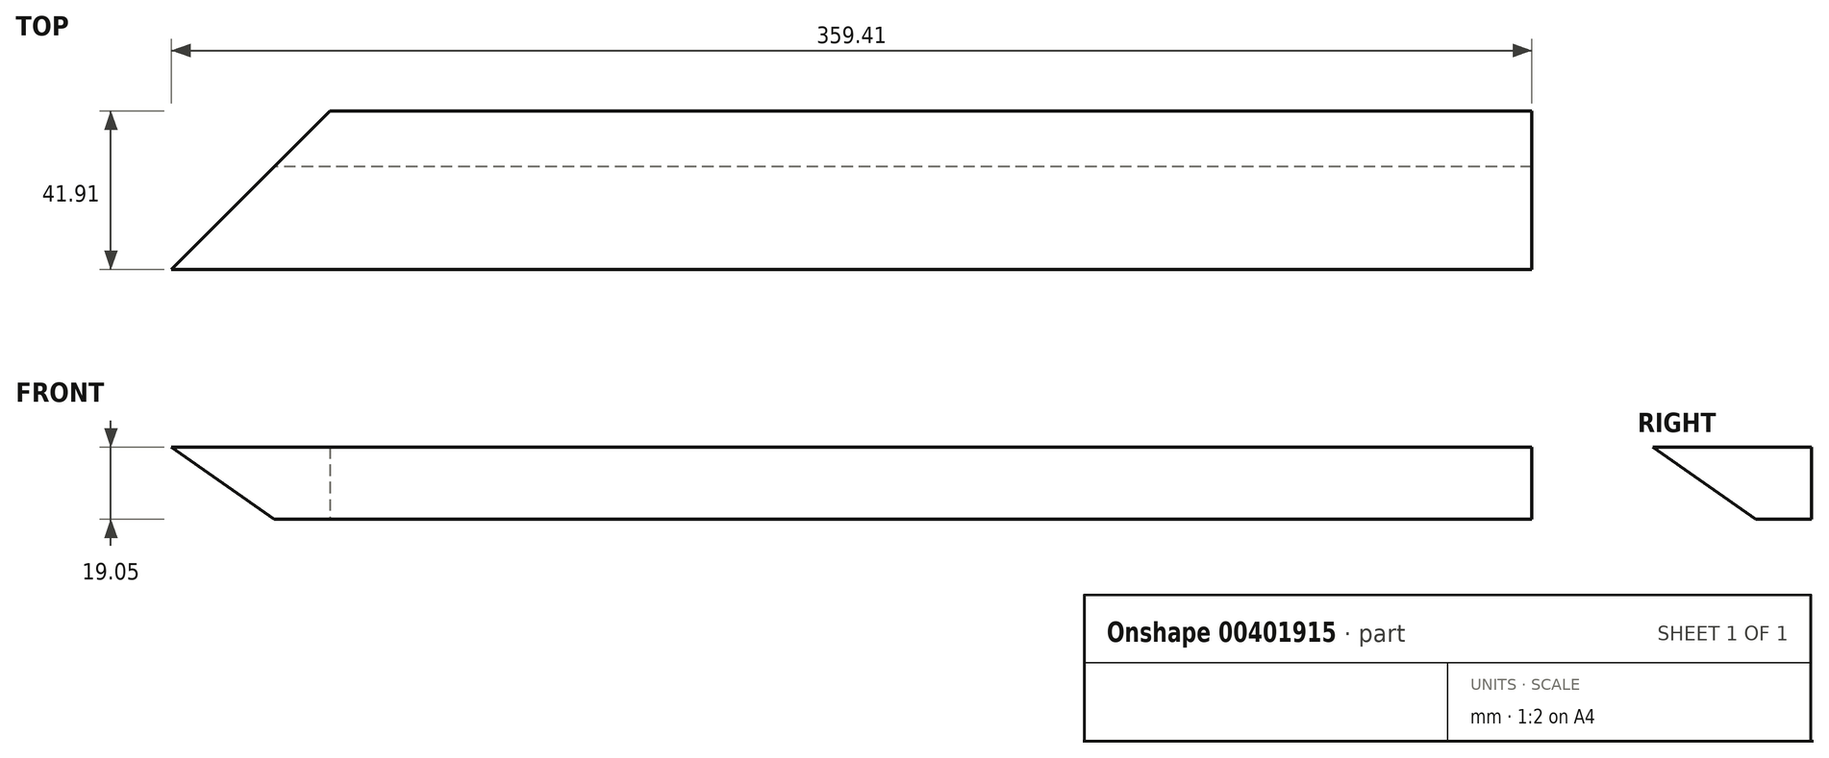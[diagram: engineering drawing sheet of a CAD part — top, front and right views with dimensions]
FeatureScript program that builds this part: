
annotation { "Feature Type Name" : "Feature", "Feature Type Description" : "" }
export const myFeature = defineFeature(function(context is Context, id is Id, definition is map)
    precondition{}
    {
        {
            var Q0;
            Q0=qCreatedBy(makeId("Right.planeOp"),FACE);
            var sketch = newSketch(context, id + "F0", { "sketchPlane" : qUnion([Q0])});
            skLineSegment(sketch, "E0.bottom", {"start": v(0, 19.05) * mm, "end": v(-41.91, 19.05) * mm});
            skLineSegment(sketch, "E0.top", {"start": v(0, 0) * mm, "end": v(-14.7, 0) * mm});
            skLineSegment(sketch, "E0.left", {"start": v(0, 19.05) * mm, "end": v(0, 0) * mm});
            skPoint(sketch, "E0.middle", {"position": v(0, 0) * mm});
            skLineSegment(sketch, "E1", {"start": v(-41.91, 19.05) * mm, "end": v(-14.7, 0) * mm});
            skSolve(sketch);
        }
        {
            var Q0;
            Q0=qSketchRegion(id+"F0",true);
            var Q1;
            Q1=qSketchRegion(id+"F2",true);
            extrude(context, id + "F1", {"entities" : qUnion([Q0, Q1]), "depth" : 228.6 * mm, "hasSecondDirection" : true, "secondDirectionOppositeDirection" : true, "secondDirectionDepth" : 228.6 * mm});
        }
        {
            var Q0;
            Q0=qCreatedBy(makeId("Top.planeOp"),FACE);
            var sketch = newSketch(context, id + "F2", { "sketchPlane" : qUnion([Q0])});
            skLineSegment(sketch, "E2", {"start": v(-88.9, 0) * mm, "end": v(88.9, 0) * mm, "construction": true});
            skLineSegment(sketch, "E3", {"start": v(0, 0) * mm, "end": v(0, -29.83) * mm, "construction": true});
            skLineSegment(sketch, "E4", {"start": v(-88.9, 0) * mm, "end": v(-237.74, 0) * mm});
            skLineSegment(sketch, "E5", {"start": v(-237.74, 0) * mm, "end": v(-237.74, -148.84) * mm});
            skLineSegment(sketch, "E6", {"start": v(-237.74, -148.84) * mm, "end": v(-88.9, 0) * mm});
            skSolve(sketch);
        }
        {
            var Q0;
            Q0=qSketchRegion(id+"F2",true);
            extrude(context, id + "F3", {"entities" : qUnion([Q0]), "operationType" : NewBodyOperationType.REMOVE, "endBound" : BoundingType.THROUGH_ALL, "depth" : 25.4 * mm});
        }
    });
